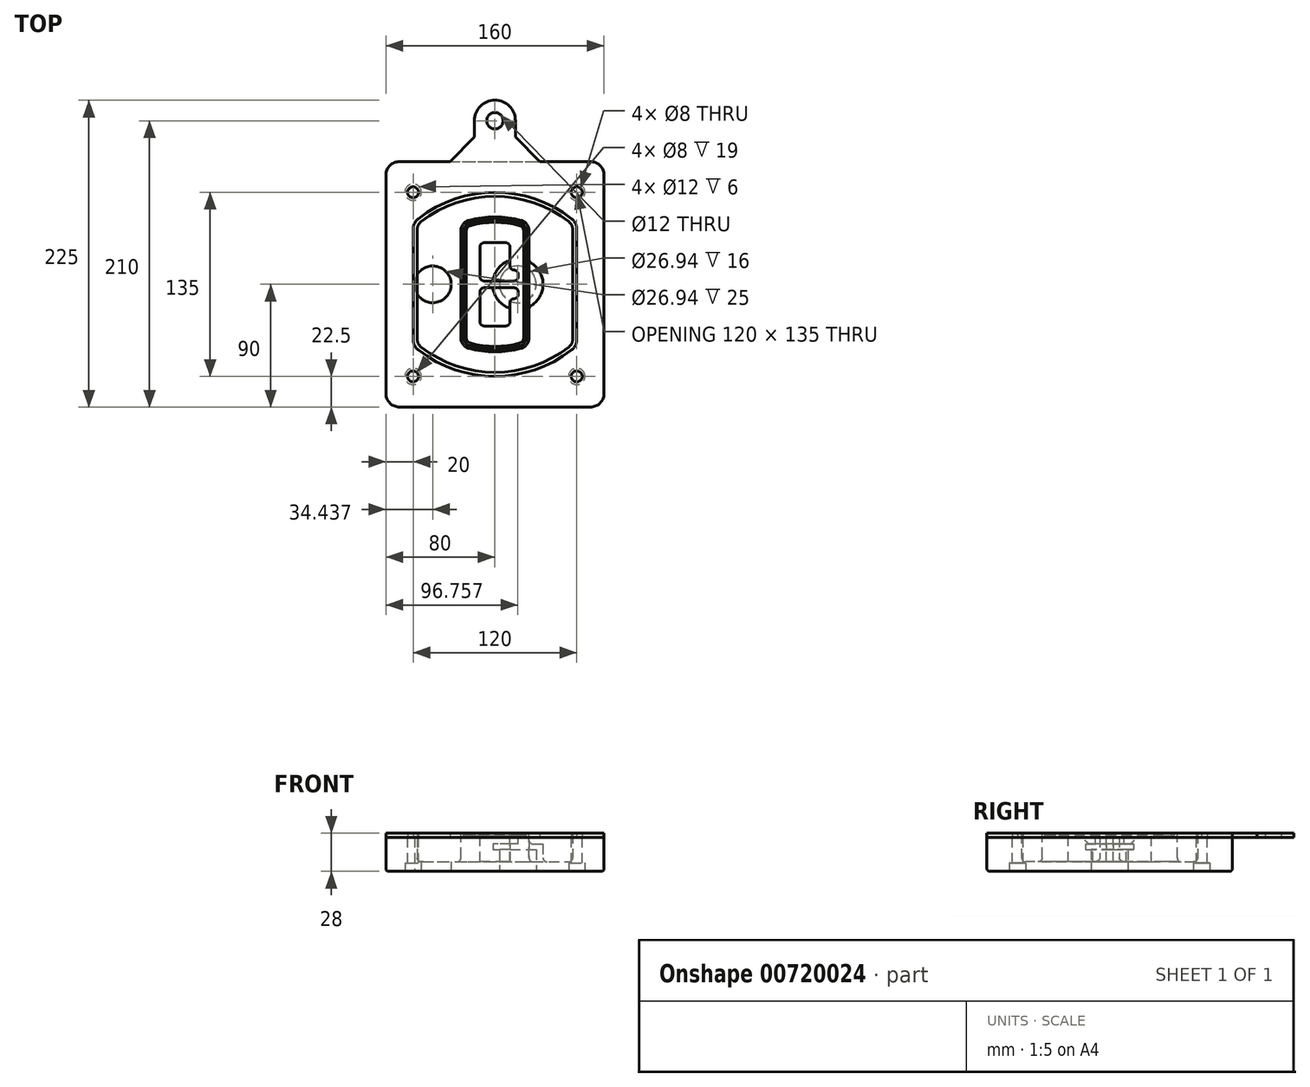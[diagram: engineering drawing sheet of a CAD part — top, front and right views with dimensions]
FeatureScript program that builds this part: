
annotation { "Feature Type Name" : "Feature", "Feature Type Description" : "" }
export const myFeature = defineFeature(function(context is Context, id is Id, definition is map)
    precondition{}
    {
        {
            var Q0;
            Q0=qCreatedBy(makeId("Top.planeOp"),FACE);
            var sketch = newSketch(context, id + "F0", { "sketchPlane" : qUnion([Q0])});
            skPoint(sketch, "E0.rect.middle", {"position": v(0, 0) * mm});
            skLineSegment(sketch, "E1.bottom", {"start": v(-70, -90) * mm, "end": v(70, -90) * mm});
            skLineSegment(sketch, "E1.top", {"start": v(-70, 90) * mm, "end": v(70, 90) * mm});
            skLineSegment(sketch, "E1.left", {"start": v(-80, -80) * mm, "end": v(-80, 80) * mm});
            skLineSegment(sketch, "E1.right", {"start": v(80, -80) * mm, "end": v(80, 80) * mm});
            skLineSegment(sketch, "E2", {"start": v(-80, 90) * mm, "end": v(80, -90) * mm, "construction": true});
            skLineSegment(sketch, "E3", {"start": v(80, 90) * mm, "end": v(-80, -90) * mm, "construction": true});
            skCircle(sketch, "E4", {"center": v(-60, 67.5) * mm, "radius": 4 * mm});
            skCircle(sketch, "E5", {"center": v(60, 67.5) * mm, "radius": 4 * mm});
            skCircle(sketch, "E6", {"center": v(60, -67.5) * mm, "radius": 4 * mm});
            skCircle(sketch, "E7", {"center": v(-60, -67.5) * mm, "radius": 4 * mm});
            skLineSegment(sketch, "E8", {"start": v(-60, 67.5) * mm, "end": v(60, 67.5) * mm, "construction": true});
            skLineSegment(sketch, "E9", {"start": v(60, 67.5) * mm, "end": v(60, -67.5) * mm, "construction": true});
            skLineSegment(sketch, "E10", {"start": v(60, -67.5) * mm, "end": v(-60, -67.5) * mm, "construction": true});
            skLineSegment(sketch, "E11", {"start": v(-60, -67.5) * mm, "end": v(-60, 67.5) * mm, "construction": true});
            skLineSegment(sketch, "E12", {"start": v(-60, 40.3) * mm, "end": v(-60, -40.3) * mm});
            skLineSegment(sketch, "E13", {"start": v(60, 40.3) * mm, "end": v(60, -40.3) * mm});
            skArc(sketch, "E14", {"start": v(56.15, 48.18) * mm, "mid": v(0, 67.5) * mm, "end": v(-56.15, 48.18) * mm});
            skArc(sketch, "E15", {"start": v(-56.15, -48.18) * mm, "mid": v(0, -67.5) * mm, "end": v(56.15, -48.18) * mm});
            skLineSegment(sketch, "E16", {"start": v(-60, 0) * mm, "end": v(60, 0) * mm, "construction": true});
            skPoint(sketch, "E17.visualSharp", {"position": v(-60, -45) * mm});
            skArc(sketch, "E17.filletArc", {"start": v(-60, -40.3) * mm, "mid": v(-58.99, -44.68) * mm, "end": v(-56.15, -48.18) * mm});
            skPoint(sketch, "E18.visualSharp", {"position": v(-60, 45) * mm});
            skArc(sketch, "E18.filletArc", {"start": v(-56.15, 48.18) * mm, "mid": v(-58.99, 44.68) * mm, "end": v(-60, 40.3) * mm});
            skPoint(sketch, "E19.visualSharp", {"position": v(60, 45) * mm});
            skArc(sketch, "E19.filletArc", {"start": v(60, 40.3) * mm, "mid": v(58.99, 44.68) * mm, "end": v(56.15, 48.18) * mm});
            skPoint(sketch, "E20.visualSharp", {"position": v(60, -45) * mm});
            skArc(sketch, "E20.filletArc", {"start": v(56.15, -48.18) * mm, "mid": v(58.99, -44.68) * mm, "end": v(60, -40.3) * mm});
            skPoint(sketch, "E21.visualSharp", {"position": v(-80, 90) * mm});
            skArc(sketch, "E21.filletArc", {"start": v(-70, 90) * mm, "mid": v(-77.07, 87.07) * mm, "end": v(-80, 80) * mm});
            skPoint(sketch, "E22.visualSharp", {"position": v(80, 90) * mm});
            skArc(sketch, "E22.filletArc", {"start": v(80, 80) * mm, "mid": v(77.07, 87.07) * mm, "end": v(70, 90) * mm});
            skPoint(sketch, "E23.visualSharp", {"position": v(80, -90) * mm});
            skArc(sketch, "E23.filletArc", {"start": v(70, -90) * mm, "mid": v(77.07, -87.07) * mm, "end": v(80, -80) * mm});
            skPoint(sketch, "E24.visualSharp", {"position": v(-80, -90) * mm});
            skArc(sketch, "E24.filletArc", {"start": v(-80, -80) * mm, "mid": v(-77.07, -87.07) * mm, "end": v(-70, -90) * mm});
            skArc(sketch, "E25.0", {"start": v(57, 40.3) * mm, "mid": v(56.3, 43.36) * mm, "end": v(54.3, 45.81) * mm});
            skLineSegment(sketch, "E25.1", {"start": v(57, 40.3) * mm, "end": v(57, -40.3) * mm});
            skArc(sketch, "E25.2", {"start": v(54.3, -45.81) * mm, "mid": v(56.3, -43.36) * mm, "end": v(57, -40.3) * mm});
            skArc(sketch, "E25.3", {"start": v(-54.3, -45.81) * mm, "mid": v(0, -64.5) * mm, "end": v(54.3, -45.81) * mm});
            skArc(sketch, "E25.4", {"start": v(-57, -40.3) * mm, "mid": v(-56.3, -43.36) * mm, "end": v(-54.3, -45.81) * mm});
            skArc(sketch, "E25.5", {"start": v(54.3, 45.81) * mm, "mid": v(0, 64.5) * mm, "end": v(-54.3, 45.81) * mm});
            skLineSegment(sketch, "E25.6", {"start": v(-57, 40.3) * mm, "end": v(-57, -40.3) * mm});
            skArc(sketch, "E25.7", {"start": v(-54.3, 45.81) * mm, "mid": v(-56.3, 43.36) * mm, "end": v(-57, 40.3) * mm});
            skArc(sketch, "E26.0", {"start": v(-58.62, 51.33) * mm, "mid": v(-62.58, 46.43) * mm, "end": v(-64, 40.3) * mm});
            skArc(sketch, "E26.1", {"start": v(58.62, 51.33) * mm, "mid": v(0, 71.5) * mm, "end": v(-58.62, 51.33) * mm});
            skArc(sketch, "E26.2", {"start": v(64, 40.3) * mm, "mid": v(62.58, 46.43) * mm, "end": v(58.62, 51.33) * mm});
            skLineSegment(sketch, "E26.3", {"start": v(64, 40.3) * mm, "end": v(64, -40.3) * mm});
            skArc(sketch, "E26.4", {"start": v(58.62, -51.33) * mm, "mid": v(62.58, -46.43) * mm, "end": v(64, -40.3) * mm});
            skLineSegment(sketch, "E26.5", {"start": v(-64, 40.3) * mm, "end": v(-64, -40.3) * mm});
            skArc(sketch, "E26.6", {"start": v(-58.62, -51.33) * mm, "mid": v(0, -71.5) * mm, "end": v(58.62, -51.33) * mm});
            skArc(sketch, "E26.7", {"start": v(-64, -40.3) * mm, "mid": v(-62.58, -46.43) * mm, "end": v(-58.62, -51.33) * mm});
            skSolve(sketch);
        }
        {
            var Q0;
            Q0=makeQuery(id+"F0.imprint","IMPRINT",FACE,{"disambiguationData":[TD([[makeQuery(id+"F0.imprint","IMPRINT",EDGE,{"derivedFrom":sQuery(id+"F0.wireOp",EDGE,"E1.bottom")}),1.0]])]});
            var Q1;
            Q1=makeQuery(id+"F0.imprint","IMPRINT",FACE,{"disambiguationData":[TD([[makeQuery(id+"F0.imprint","IMPRINT",EDGE,{"derivedFrom":sQuery(id+"F0.wireOp",EDGE,"E12")}),1.0]])]});
            var Q2;
            Q2=makeQuery(id+"F0.imprint","IMPRINT",FACE,{"disambiguationData":[TD([[makeQuery(id+"F0.imprint","IMPRINT",EDGE,{"derivedFrom":sQuery(id+"F0.wireOp",EDGE,"E25.0")}),1.0]])]});
            var Q3;
            Q3=makeQuery(id+"F0.imprint","IMPRINT",FACE,{"disambiguationData":[TD([[makeQuery(id+"F0.imprint","IMPRINT",EDGE,{"derivedFrom":sQuery(id+"F0.wireOp",EDGE,"E12")}),-1.0]])]});
            extrude(context, id + "F1", {"entities" : qUnion([Q0, Q1, Q2, Q3]), "oppositeDirection" : true, "depth" : 25 * mm});
        }
        {
            var Q0;
            Q0=makeQuery(id+"F0.imprint","IMPRINT",FACE,{"disambiguationData":[TD([[makeQuery(id+"F0.imprint","IMPRINT",EDGE,{"derivedFrom":sQuery(id+"F0.wireOp",EDGE,"E12")}),1.0]])]});
            extrude(context, id + "F2", {"entities" : qUnion([Q0]), "operationType" : NewBodyOperationType.ADD, "depth" : 3 * mm});
        }
        {
            var Q0;
            Q0=makeQuery(id+"F0.imprint","IMPRINT",FACE,{"disambiguationData":[TD([[makeQuery(id+"F0.imprint","IMPRINT",EDGE,{"derivedFrom":sQuery(id+"F0.wireOp",EDGE,"E25.0")}),1.0]])]});
            extrude(context, id + "F3", {"entities" : qUnion([Q0]), "operationType" : NewBodyOperationType.REMOVE, "oppositeDirection" : true, "depth" : 18 * mm});
        }
        {
            var Q0;
            Q0=makeQuery(id+"F2.opExtrude","CAP_FACE",FACE,{"disambiguationData":[OSD([sQuery(id+"F0.wireOp",EDGE,"E12"),sQuery(id+"F0.wireOp",EDGE,"E13"),sQuery(id+"F0.wireOp",EDGE,"E14"),sQuery(id+"F0.wireOp",EDGE,"E15"),sQuery(id+"F0.wireOp",EDGE,"E17.filletArc"),sQuery(id+"F0.wireOp",EDGE,"E18.filletArc"),sQuery(id+"F0.wireOp",EDGE,"E19.filletArc"),sQuery(id+"F0.wireOp",EDGE,"E20.filletArc"),sQuery(id+"F0.wireOp",EDGE,"E25.0"),sQuery(id+"F0.wireOp",EDGE,"E25.1"),sQuery(id+"F0.wireOp",EDGE,"E25.2"),sQuery(id+"F0.wireOp",EDGE,"E25.3"),sQuery(id+"F0.wireOp",EDGE,"E25.4"),sQuery(id+"F0.wireOp",EDGE,"E25.5"),sQuery(id+"F0.wireOp",EDGE,"E25.6"),sQuery(id+"F0.wireOp",EDGE,"E25.7")])],"isStart":false});
            var sketch = newSketch(context, id + "F4", { "sketchPlane" : qUnion([Q0])});
            skArc(sketch, "E27.0", {"start": v(-19.08, -46.97) * mm, "mid": v(0, -49.5) * mm, "end": v(19.08, -46.97) * mm});
            skArc(sketch, "E28.0", {"start": v(19.08, 46.97) * mm, "mid": v(0, 49.5) * mm, "end": v(-19.08, 46.97) * mm});
            skLineSegment(sketch, "E29", {"start": v(-25, 39.25) * mm, "end": v(-25, -39.25) * mm});
            skLineSegment(sketch, "E30", {"start": v(25, 39.25) * mm, "end": v(25, -39.25) * mm});
            skLineSegment(sketch, "E31", {"start": v(-25, 45.1) * mm, "end": v(25, 45.1) * mm, "construction": true});
            skLineSegment(sketch, "E32", {"start": v(-25, -45.1) * mm, "end": v(25, -45.1) * mm, "construction": true});
            skPoint(sketch, "E33.visualSharp", {"position": v(-25, 45.1) * mm});
            skArc(sketch, "E33.filletArc", {"start": v(-19.08, 46.97) * mm, "mid": v(-23.35, 44.11) * mm, "end": v(-25, 39.25) * mm});
            skPoint(sketch, "E34.visualSharp", {"position": v(25, 45.1) * mm});
            skArc(sketch, "E34.filletArc", {"start": v(25, 39.25) * mm, "mid": v(23.35, 44.11) * mm, "end": v(19.08, 46.97) * mm});
            skPoint(sketch, "E35.visualSharp", {"position": v(25, -45.1) * mm});
            skArc(sketch, "E35.filletArc", {"start": v(19.08, -46.97) * mm, "mid": v(23.35, -44.11) * mm, "end": v(25, -39.25) * mm});
            skPoint(sketch, "E36.visualSharp", {"position": v(-25, -45.1) * mm});
            skArc(sketch, "E36.filletArc", {"start": v(-25, -39.25) * mm, "mid": v(-23.35, -44.11) * mm, "end": v(-19.08, -46.97) * mm});
            skArc(sketch, "E37.0", {"start": v(54.3, 45.81) * mm, "mid": v(0, 64.5) * mm, "end": v(-54.3, 45.81) * mm});
            skArc(sketch, "E37.1", {"start": v(-54.3, 45.81) * mm, "mid": v(-56.3, 43.36) * mm, "end": v(-57, 40.3) * mm});
            skLineSegment(sketch, "E37.2", {"start": v(-57, 40.3) * mm, "end": v(-57, -40.3) * mm});
            skArc(sketch, "E37.3", {"start": v(-57, -40.3) * mm, "mid": v(-56.3, -43.36) * mm, "end": v(-54.3, -45.81) * mm});
            skArc(sketch, "E37.4", {"start": v(-54.3, -45.81) * mm, "mid": v(0, -64.5) * mm, "end": v(54.3, -45.81) * mm});
            skArc(sketch, "E37.5", {"start": v(54.3, -45.81) * mm, "mid": v(56.3, -43.36) * mm, "end": v(57, -40.3) * mm});
            skLineSegment(sketch, "E37.6", {"start": v(57, 40.3) * mm, "end": v(57, -40.3) * mm});
            skArc(sketch, "E37.7", {"start": v(57, 40.3) * mm, "mid": v(56.3, 43.36) * mm, "end": v(54.3, 45.81) * mm});
            skLineSegment(sketch, "E38.0", {"start": v(23, 39.25) * mm, "end": v(23, -39.25) * mm});
            skArc(sketch, "E38.1", {"start": v(18.56, -45.04) * mm, "mid": v(21.76, -42.9) * mm, "end": v(23, -39.25) * mm});
            skArc(sketch, "E38.2", {"start": v(-18.56, -45.04) * mm, "mid": v(0, -47.5) * mm, "end": v(18.56, -45.04) * mm});
            skArc(sketch, "E38.3", {"start": v(-23, -39.25) * mm, "mid": v(-21.76, -42.9) * mm, "end": v(-18.56, -45.04) * mm});
            skLineSegment(sketch, "E38.4", {"start": v(-23, 39.25) * mm, "end": v(-23, -39.25) * mm});
            skArc(sketch, "E38.5", {"start": v(23, 39.25) * mm, "mid": v(21.76, 42.9) * mm, "end": v(18.56, 45.04) * mm});
            skArc(sketch, "E38.6", {"start": v(-18.56, 45.04) * mm, "mid": v(-21.76, 42.9) * mm, "end": v(-23, 39.25) * mm});
            skArc(sketch, "E38.7", {"start": v(18.56, 45.04) * mm, "mid": v(0, 47.5) * mm, "end": v(-18.56, 45.04) * mm});
            skArc(sketch, "E39.0", {"start": v(21, 39.25) * mm, "mid": v(20.18, 41.68) * mm, "end": v(18.04, 43.1) * mm});
            skLineSegment(sketch, "E39.1", {"start": v(21, 39.25) * mm, "end": v(21, -39.25) * mm});
            skArc(sketch, "E39.2", {"start": v(18.04, -43.1) * mm, "mid": v(20.18, -41.68) * mm, "end": v(21, -39.25) * mm});
            skArc(sketch, "E39.3", {"start": v(-18.04, -43.1) * mm, "mid": v(0, -45.5) * mm, "end": v(18.04, -43.1) * mm});
            skArc(sketch, "E39.4", {"start": v(-21, -39.25) * mm, "mid": v(-20.18, -41.68) * mm, "end": v(-18.04, -43.1) * mm});
            skArc(sketch, "E39.5", {"start": v(18.04, 43.1) * mm, "mid": v(0, 45.5) * mm, "end": v(-18.04, 43.1) * mm});
            skLineSegment(sketch, "E39.6", {"start": v(-21, 39.25) * mm, "end": v(-21, -39.25) * mm});
            skArc(sketch, "E39.7", {"start": v(-18.04, 43.1) * mm, "mid": v(-20.18, 41.68) * mm, "end": v(-21, 39.25) * mm});
            skLineSegment(sketch, "E40", {"start": v(-25, 0) * mm, "end": v(25, 0) * mm, "construction": true});
            skLineSegment(sketch, "E41", {"start": v(-11, 5.5) * mm, "end": v(-11, 27.5) * mm});
            skLineSegment(sketch, "E42", {"start": v(-8, 30.5) * mm, "end": v(8, 30.5) * mm});
            skLineSegment(sketch, "E43", {"start": v(11, 27.5) * mm, "end": v(11, 13.5) * mm});
            skLineSegment(sketch, "E44", {"start": v(14, 10.5) * mm, "end": v(14, 10.5) * mm});
            skLineSegment(sketch, "E45", {"start": v(17, 7.5) * mm, "end": v(17, 5.5) * mm});
            skLineSegment(sketch, "E46", {"start": v(14, 2.5) * mm, "end": v(-8, 2.5) * mm});
            skPoint(sketch, "E47.visualSharp", {"position": v(-11, 30.5) * mm});
            skArc(sketch, "E47.filletArc", {"start": v(-8, 30.5) * mm, "mid": v(-10.12, 29.62) * mm, "end": v(-11, 27.5) * mm});
            skPoint(sketch, "E48.visualSharp", {"position": v(11, 30.5) * mm});
            skArc(sketch, "E48.filletArc", {"start": v(11, 27.5) * mm, "mid": v(10.12, 29.62) * mm, "end": v(8, 30.5) * mm});
            skPoint(sketch, "E49.visualSharp", {"position": v(11, 10.5) * mm});
            skArc(sketch, "E49.filletArc", {"start": v(11, 13.5) * mm, "mid": v(11.88, 11.38) * mm, "end": v(14, 10.5) * mm});
            skPoint(sketch, "E50.visualSharp", {"position": v(17, 10.5) * mm});
            skArc(sketch, "E50.filletArc", {"start": v(17, 7.5) * mm, "mid": v(16.12, 9.62) * mm, "end": v(14, 10.5) * mm});
            skPoint(sketch, "E51.visualSharp", {"position": v(17, 2.5) * mm});
            skArc(sketch, "E51.filletArc", {"start": v(14, 2.5) * mm, "mid": v(16.12, 3.38) * mm, "end": v(17, 5.5) * mm});
            skPoint(sketch, "E52.visualSharp", {"position": v(-11, 2.5) * mm});
            skArc(sketch, "E52.filletArc", {"start": v(-11, 5.5) * mm, "mid": v(-10.12, 3.38) * mm, "end": v(-8, 2.5) * mm});
            skLineSegment(sketch, "E53.0.MirrorCS", {"start": v(14, -2.5) * mm, "end": v(-8, -2.5) * mm});
            skArc(sketch, "E54.0.MirrorCS", {"start": v(-11, -5.5) * mm, "mid": v(-10.12, -3.38) * mm, "end": v(-8, -2.5) * mm});
            skLineSegment(sketch, "E55.0.MirrorCS", {"start": v(-11, -5.5) * mm, "end": v(-11, -27.5) * mm});
            skArc(sketch, "E56.0.MirrorCS", {"start": v(-8, -30.5) * mm, "mid": v(-10.12, -29.62) * mm, "end": v(-11, -27.5) * mm});
            skLineSegment(sketch, "E57.0.MirrorCS", {"start": v(-8, -30.5) * mm, "end": v(8, -30.5) * mm});
            skArc(sketch, "E58.0.MirrorCS", {"start": v(11, -27.5) * mm, "mid": v(10.12, -29.62) * mm, "end": v(8, -30.5) * mm});
            skLineSegment(sketch, "E59.0.MirrorCS", {"start": v(11, -27.5) * mm, "end": v(11, -13.5) * mm});
            skArc(sketch, "E60.0.MirrorCS", {"start": v(11, -13.5) * mm, "mid": v(11.88, -11.38) * mm, "end": v(14, -10.5) * mm});
            skArc(sketch, "E61.0.MirrorCS", {"start": v(17, -7.5) * mm, "mid": v(16.12, -9.62) * mm, "end": v(14, -10.5) * mm});
            skLineSegment(sketch, "E62.0.MirrorCS", {"start": v(17, -7.5) * mm, "end": v(17, -5.5) * mm});
            skArc(sketch, "E63.0.MirrorCS", {"start": v(14, -2.5) * mm, "mid": v(16.12, -3.38) * mm, "end": v(17, -5.5) * mm});
            skSolve(sketch);
        }
        {
            var Q0;
            Q0=makeQuery(id+"F4.imprint","IMPRINT",FACE,{"disambiguationData":[TD([[makeQuery(id+"F4.imprint","IMPRINT",EDGE,{"derivedFrom":sQuery(id+"F4.wireOp",EDGE,"E27.0")}),1.0]])]});
            var Q1;
            Q1=makeQuery(id+"F4.imprint","IMPRINT",FACE,{"disambiguationData":[TD([[makeQuery(id+"F4.imprint","IMPRINT",EDGE,{"derivedFrom":sQuery(id+"F4.wireOp",EDGE,"E38.0")}),-1.0]])]});
            var Q2;
            Q2=makeQuery(id+"F4.imprint","IMPRINT",FACE,{"disambiguationData":[TD([[makeQuery(id+"F4.imprint","IMPRINT",EDGE,{"derivedFrom":sQuery(id+"F4.wireOp",EDGE,"E39.0")}),1.0]])]});
            extrude(context, id + "F5", {"entities" : qUnion([Q0, Q1, Q2]), "operationType" : NewBodyOperationType.ADD, "endBound" : BoundingType.UP_TO_NEXT, "oppositeDirection" : true, "depth" : 25 * mm});
        }
        {
            var Q0;
            Q0=makeQuery(id+"F4.imprint","IMPRINT",FACE,{"disambiguationData":[TD([[makeQuery(id+"F4.imprint","IMPRINT",EDGE,{"derivedFrom":sQuery(id+"F4.wireOp",EDGE,"E38.0")}),-1.0]])]});
            extrude(context, id + "F6", {"entities" : qUnion([Q0]), "operationType" : NewBodyOperationType.REMOVE, "oppositeDirection" : true, "depth" : 2 * mm});
        }
        {
            var Q0;
            Q0=makeQuery(id+"F1.opExtrude","CAP_FACE",FACE,{"disambiguationData":[OSD([sQuery(id+"F0.wireOp",EDGE,"E1.bottom"),sQuery(id+"F0.wireOp",EDGE,"E1.top"),sQuery(id+"F0.wireOp",EDGE,"E1.left"),sQuery(id+"F0.wireOp",EDGE,"E1.right"),sQuery(id+"F0.wireOp",EDGE,"E4"),sQuery(id+"F0.wireOp",EDGE,"E5"),sQuery(id+"F0.wireOp",EDGE,"E6"),sQuery(id+"F0.wireOp",EDGE,"E7"),sQuery(id+"F0.wireOp",EDGE,"E21.filletArc"),sQuery(id+"F0.wireOp",EDGE,"E22.filletArc"),sQuery(id+"F0.wireOp",EDGE,"E23.filletArc"),sQuery(id+"F0.wireOp",EDGE,"E24.filletArc")])],"isStart":false});
            var sketch = newSketch(context, id + "F7", { "sketchPlane" : qUnion([Q0])});
            skCircle(sketch, "E64", {"center": v(16.76, 0) * mm, "radius": 13.47 * mm});
            skCircle(sketch, "E65", {"center": v(-45.56, 0) * mm, "radius": 13.47 * mm});
            skLineSegment(sketch, "E66", {"start": v(80, 0) * mm, "end": v(-80, 0) * mm});
            skCircle(sketch, "E67", {"center": v(16.76, 0) * mm, "radius": 18.47 * mm});
            skCircle(sketch, "E68", {"center": v(60, -67.5) * mm, "radius": 6 * mm});
            skCircle(sketch, "E69", {"center": v(-60, -67.5) * mm, "radius": 6 * mm});
            skCircle(sketch, "E70", {"center": v(-60, 67.5) * mm, "radius": 6 * mm});
            skCircle(sketch, "E71", {"center": v(60, 67.5) * mm, "radius": 6 * mm});
            skSolve(sketch);
        }
        {
            var Q0;
            {var subQ1=sQuery(id+"F7.wireOp",EDGE,"E66");var subQ4=sQuery(id+"F7.wireOp",EDGE,"E64");var subQ6=makeQuery(id+"F7.imprint","INTERSECT",VERTEX,{"disambiguationData":[OD(0.0)],"derivedFrom":[subQ4,subQ1]});Q0=makeQuery(id+"F7.imprint","IMPRINT",FACE,{"disambiguationData":[TD([[makeQuery(id+"F7.imprint","IMPRINT",EDGE,{"disambiguationData":[TD([[subQ6,-1.0]])],"derivedFrom":subQ4}),-1.0]])]});}
            var Q1;
            {var subQ0=sQuery(id+"F7.wireOp",EDGE,"E66");var subQ1=sQuery(id+"F7.wireOp",EDGE,"E64");var subQ3=makeQuery(id+"F7.imprint","INTERSECT",VERTEX,{"disambiguationData":[OD(0.0)],"derivedFrom":[subQ1,subQ0]});Q1=makeQuery(id+"F7.imprint","IMPRINT",FACE,{"disambiguationData":[TD([[makeQuery(id+"F7.imprint","IMPRINT",EDGE,{"disambiguationData":[TD([[subQ3,-1.0]])],"derivedFrom":subQ1}),1.0]])]});}
            var Q2;
            {var subQ0=sQuery(id+"F7.wireOp",EDGE,"E66");var subQ1=sQuery(id+"F7.wireOp",EDGE,"E64");var subQ3=makeQuery(id+"F7.imprint","INTERSECT",VERTEX,{"disambiguationData":[OD(0.0)],"derivedFrom":[subQ1,subQ0]});Q2=makeQuery(id+"F7.imprint","IMPRINT",FACE,{"disambiguationData":[TD([[makeQuery(id+"F7.imprint","IMPRINT",EDGE,{"disambiguationData":[TD([[subQ3,1.0]])],"derivedFrom":subQ1}),1.0]])]});}
            var Q3;
            {var subQ1=sQuery(id+"F7.wireOp",EDGE,"E66");var subQ4=sQuery(id+"F7.wireOp",EDGE,"E64");var subQ6=makeQuery(id+"F7.imprint","INTERSECT",VERTEX,{"disambiguationData":[OD(0.0)],"derivedFrom":[subQ4,subQ1]});Q3=makeQuery(id+"F7.imprint","IMPRINT",FACE,{"disambiguationData":[TD([[makeQuery(id+"F7.imprint","IMPRINT",EDGE,{"disambiguationData":[TD([[subQ6,1.0]])],"derivedFrom":subQ4}),-1.0]])]});}
            extrude(context, id + "F8", {"entities" : qUnion([Q0, Q1, Q2, Q3]), "operationType" : NewBodyOperationType.ADD, "oppositeDirection" : true, "depth" : 20 * mm});
        }
        {
            var Q0;
            {var subQ0=sQuery(id+"F7.wireOp",EDGE,"E66");var subQ1=sQuery(id+"F7.wireOp",EDGE,"E64");var subQ3=makeQuery(id+"F7.imprint","INTERSECT",VERTEX,{"disambiguationData":[OD(0.0)],"derivedFrom":[subQ1,subQ0]});Q0=makeQuery(id+"F7.imprint","IMPRINT",FACE,{"disambiguationData":[TD([[makeQuery(id+"F7.imprint","IMPRINT",EDGE,{"disambiguationData":[TD([[subQ3,-1.0]])],"derivedFrom":subQ1}),1.0]])]});}
            var Q1;
            {var subQ0=sQuery(id+"F7.wireOp",EDGE,"E66");var subQ1=sQuery(id+"F7.wireOp",EDGE,"E64");var subQ3=makeQuery(id+"F7.imprint","INTERSECT",VERTEX,{"disambiguationData":[OD(0.0)],"derivedFrom":[subQ1,subQ0]});Q1=makeQuery(id+"F7.imprint","IMPRINT",FACE,{"disambiguationData":[TD([[makeQuery(id+"F7.imprint","IMPRINT",EDGE,{"disambiguationData":[TD([[subQ3,1.0]])],"derivedFrom":subQ1}),1.0]])]});}
            extrude(context, id + "F9", {"entities" : qUnion([Q0, Q1]), "operationType" : NewBodyOperationType.REMOVE, "oppositeDirection" : true, "depth" : 16 * mm});
        }
        {
            var Q0;
            {var subQ0=sQuery(id+"F7.wireOp",EDGE,"E66");var subQ1=sQuery(id+"F7.wireOp",EDGE,"E65");var subQ3=makeQuery(id+"F7.imprint","INTERSECT",VERTEX,{"disambiguationData":[OD(0.0)],"derivedFrom":[subQ1,subQ0]});Q0=makeQuery(id+"F7.imprint","IMPRINT",FACE,{"disambiguationData":[TD([[makeQuery(id+"F7.imprint","IMPRINT",EDGE,{"disambiguationData":[TD([[subQ3,-1.0]])],"derivedFrom":subQ1}),1.0]])]});}
            var Q1;
            {var subQ0=sQuery(id+"F7.wireOp",EDGE,"E66");var subQ1=sQuery(id+"F7.wireOp",EDGE,"E65");var subQ3=makeQuery(id+"F7.imprint","INTERSECT",VERTEX,{"disambiguationData":[OD(0.0)],"derivedFrom":[subQ1,subQ0]});Q1=makeQuery(id+"F7.imprint","IMPRINT",FACE,{"disambiguationData":[TD([[makeQuery(id+"F7.imprint","IMPRINT",EDGE,{"disambiguationData":[TD([[subQ3,1.0]])],"derivedFrom":subQ1}),1.0]])]});}
            extrude(context, id + "F10", {"entities" : qUnion([Q0, Q1]), "operationType" : NewBodyOperationType.REMOVE, "oppositeDirection" : true, "depth" : 25 * mm});
        }
        {
            var Q0;
            Q0=makeQuery(id+"F7.imprint","IMPRINT",FACE,{"disambiguationData":[TD([[makeQuery(id+"F7.imprint","IMPRINT",EDGE,{"derivedFrom":sQuery(id+"F7.wireOp",EDGE,"E68")}),1.0]])]});
            var Q1;
            Q1=makeQuery(id+"F7.imprint","IMPRINT",FACE,{"disambiguationData":[TD([[makeQuery(id+"F7.imprint","IMPRINT",EDGE,{"derivedFrom":makeQuery(id+"F1.opExtrude","CAP_EDGE",EDGE,{"disambiguationData":[OSD([sQuery(id+"F0.wireOp",EDGE,"E5")])],"isStart":false})}),-1.0]])]});
            var Q2;
            Q2=makeQuery(id+"F7.imprint","IMPRINT",FACE,{"disambiguationData":[TD([[makeQuery(id+"F7.imprint","IMPRINT",EDGE,{"derivedFrom":sQuery(id+"F7.wireOp",EDGE,"E69")}),1.0]])]});
            var Q3;
            Q3=makeQuery(id+"F7.imprint","IMPRINT",FACE,{"disambiguationData":[TD([[makeQuery(id+"F7.imprint","IMPRINT",EDGE,{"derivedFrom":makeQuery(id+"F1.opExtrude","CAP_EDGE",EDGE,{"disambiguationData":[OSD([sQuery(id+"F0.wireOp",EDGE,"E4")])],"isStart":false})}),-1.0]])]});
            var Q4;
            Q4=makeQuery(id+"F7.imprint","IMPRINT",FACE,{"disambiguationData":[TD([[makeQuery(id+"F7.imprint","IMPRINT",EDGE,{"derivedFrom":sQuery(id+"F7.wireOp",EDGE,"E70")}),1.0]])]});
            var Q5;
            Q5=makeQuery(id+"F7.imprint","IMPRINT",FACE,{"disambiguationData":[TD([[makeQuery(id+"F7.imprint","IMPRINT",EDGE,{"derivedFrom":makeQuery(id+"F1.opExtrude","CAP_EDGE",EDGE,{"disambiguationData":[OSD([sQuery(id+"F0.wireOp",EDGE,"E7")])],"isStart":false})}),-1.0]])]});
            var Q6;
            Q6=makeQuery(id+"F7.imprint","IMPRINT",FACE,{"disambiguationData":[TD([[makeQuery(id+"F7.imprint","IMPRINT",EDGE,{"derivedFrom":sQuery(id+"F7.wireOp",EDGE,"E71")}),1.0]])]});
            var Q7;
            Q7=makeQuery(id+"F7.imprint","IMPRINT",FACE,{"disambiguationData":[TD([[makeQuery(id+"F7.imprint","IMPRINT",EDGE,{"derivedFrom":makeQuery(id+"F1.opExtrude","CAP_EDGE",EDGE,{"disambiguationData":[OSD([sQuery(id+"F0.wireOp",EDGE,"E6")])],"isStart":false})}),-1.0]])]});
            extrude(context, id + "F11", {"entities" : qUnion([Q0, Q1, Q2, Q3, Q4, Q5, Q6, Q7]), "operationType" : NewBodyOperationType.REMOVE, "oppositeDirection" : true, "depth" : 6 * mm});
        }
        {
            var Q0;
            Q0=makeQuery(id+"F9.boolean.opBoolean","COPY",FACE,{"derivedFrom":makeQuery(id+"F9.opExtrude","CAP_FACE",FACE,{"disambiguationData":[OSD([sQuery(id+"F7.wireOp",EDGE,"E64")])],"isStart":false})});
            var sketch = newSketch(context, id + "F12", { "sketchPlane" : qUnion([Q0])});
            skArc(sketch, "E72.0", {"start": v(11, 17.55) * mm, "mid": v(2.57, 11.82) * mm, "end": v(-1.54, 2.5) * mm});
            skArc(sketch, "E72.1", {"start": v(-1.54, -2.5) * mm, "mid": v(2.57, -11.82) * mm, "end": v(11, -17.55) * mm});
            skLineSegment(sketch, "E73", {"start": v(-1.54, -2.5) * mm, "end": v(14, -2.5) * mm});
            skLineSegment(sketch, "E74.0", {"start": v(14, 2.5) * mm, "end": v(-1.54, 2.5) * mm});
            skArc(sketch, "E74.1", {"start": v(14, 2.5) * mm, "mid": v(16.12, 3.38) * mm, "end": v(17, 5.5) * mm});
            skLineSegment(sketch, "E74.2", {"start": v(17, 7.5) * mm, "end": v(17, 5.5) * mm});
            skArc(sketch, "E74.3", {"start": v(17, 7.5) * mm, "mid": v(16.12, 9.62) * mm, "end": v(14, 10.5) * mm});
            skArc(sketch, "E74.4", {"start": v(11, 13.5) * mm, "mid": v(11.88, 11.38) * mm, "end": v(14, 10.5) * mm});
            skLineSegment(sketch, "E74.5", {"start": v(11, 17.55) * mm, "end": v(11, 13.5) * mm});
            skLineSegment(sketch, "E74.7", {"start": v(14, -2.5) * mm, "end": v(-1.54, -2.5) * mm});
            skArc(sketch, "E74.8", {"start": v(14, -2.5) * mm, "mid": v(16.12, -3.38) * mm, "end": v(17, -5.5) * mm});
            skLineSegment(sketch, "E74.9", {"start": v(17, -7.5) * mm, "end": v(17, -5.5) * mm});
            skArc(sketch, "E74.10", {"start": v(17, -7.5) * mm, "mid": v(16.12, -9.62) * mm, "end": v(14, -10.5) * mm});
            skArc(sketch, "E74.11", {"start": v(11, -13.5) * mm, "mid": v(11.88, -11.38) * mm, "end": v(14, -10.5) * mm});
            skLineSegment(sketch, "E74.12", {"start": v(11, -17.55) * mm, "end": v(11, -13.5) * mm});
            skPoint(sketch, "E75.orphan", {"position": v(11, -27.5) * mm});
            skPoint(sketch, "E76.orphan", {"position": v(-8, -2.5) * mm});
            skPoint(sketch, "E77.orphan", {"position": v(-8, 2.5) * mm});
            skPoint(sketch, "E78.orphan", {"position": v(11, 27.5) * mm});
            skSolve(sketch);
        }
        {
            var Q0;
            {var subQ7=sQuery(id+"F12.wireOp",EDGE,"E72.0");var subQ14=sQuery(id+"F12.wireOp",EDGE,"E72.1");var subQ16=sQuery(id+"F12.wireOp",EDGE,"E74.1");var subQ18=sQuery(id+"F12.wireOp",EDGE,"E74.8");Q0=qUnion([makeQuery(id+"F12.imprint","IMPRINT",FACE,{"disambiguationData":[TD([[makeQuery(id+"F12.imprint","IMPRINT",EDGE,{"derivedFrom":subQ7}),1.0]])]}),makeQuery(id+"F12.imprint","IMPRINT",FACE,{"disambiguationData":[TD([[makeQuery(id+"F12.imprint","IMPRINT",EDGE,{"derivedFrom":subQ14}),1.0]])]}),makeQuery(id+"F12.imprint","IMPRINT",FACE,{"disambiguationData":[TD([[makeQuery(id+"F12.imprint","IMPRINT",EDGE,{"derivedFrom":subQ16}),1.0]])]}),makeQuery(id+"F12.imprint","IMPRINT",FACE,{"disambiguationData":[TD([[makeQuery(id+"F12.imprint","IMPRINT",EDGE,{"derivedFrom":subQ18}),-1.0]])]})]);}
            var Q1;
            Q1=makeQuery(id+"F5.boolean.opBoolean","SPLIT",FACE,{"disambiguationData":[TD([makeQuery(id+"F5.opExtrude","SWEPT_FACE",FACE,{"disambiguationData":[OSD([sQuery(id+"F4.wireOp",EDGE,"E41")])]})])],"derivedFrom":makeQuery(id+"F3.boolean.opBoolean","COPY",FACE,{"derivedFrom":makeQuery(id+"F3.opExtrude","CAP_FACE",FACE,{"disambiguationData":[OSD([sQuery(id+"F0.wireOp",EDGE,"E25.0"),sQuery(id+"F0.wireOp",EDGE,"E25.1"),sQuery(id+"F0.wireOp",EDGE,"E25.2"),sQuery(id+"F0.wireOp",EDGE,"E25.3"),sQuery(id+"F0.wireOp",EDGE,"E25.4"),sQuery(id+"F0.wireOp",EDGE,"E25.5"),sQuery(id+"F0.wireOp",EDGE,"E25.6"),sQuery(id+"F0.wireOp",EDGE,"E25.7")])],"isStart":false})})});
            extrude(context, id + "F13", {"entities" : qUnion([Q0]), "operationType" : NewBodyOperationType.REMOVE, "endBound" : BoundingType.UP_TO_SURFACE, "endBoundEntityFace" : qUnion([Q1]), "depth" : 25 * mm});
        }
        {
            var Q0;
            Q0=makeQuery(id+"F3.boolean.opBoolean","COPY",EDGE,{"derivedFrom":makeQuery(id+"F3.opExtrude","CAP_EDGE",EDGE,{"disambiguationData":[OSD([sQuery(id+"F0.wireOp",EDGE,"E25.6")])],"isStart":false})});
            var Q1;
            Q1=makeQuery(id+"F8.boolean.opBoolean","INTERSECT",EDGE,{"derivedFrom":[makeQuery(id+"F5.opExtrude","SWEPT_FACE",FACE,{"disambiguationData":[OSD([sQuery(id+"F4.wireOp",EDGE,"E30")])]}),makeQuery(id+"F8.opExtrude","CAP_FACE",FACE,{"disambiguationData":[OSD([sQuery(id+"F7.wireOp",EDGE,"E67")])],"isStart":false})]});
            var Q2;
            Q2=makeQuery(id+"F8.boolean.opBoolean","INTERSECT",EDGE,{"disambiguationData":[OD(1.0)],"derivedFrom":[makeQuery(id+"F5.opExtrude","SWEPT_FACE",FACE,{"disambiguationData":[OSD([sQuery(id+"F4.wireOp",EDGE,"E30")])]}),makeQuery(id+"F8.opExtrude","SWEPT_FACE",FACE,{"disambiguationData":[OSD([sQuery(id+"F7.wireOp",EDGE,"E67")])]})]});
            var Q3;
            {var subQ0=sQuery(id+"F4.wireOp",EDGE,"E30");Q3=makeQuery(id+"F8.boolean.opBoolean","SPLIT",EDGE,{"disambiguationData":[TD([makeQuery(id+"F5.opExtrude","SWEPT_FACE",FACE,{"disambiguationData":[OSD([sQuery(id+"F4.wireOp",EDGE,"E35.filletArc")])]})])],"derivedFrom":makeQuery(id+"F5.opExtrude","CAP_EDGE",EDGE,{"disambiguationData":[OSD([subQ0])],"isStart":false})});}
            var Q4;
            {var subQ0=sQuery(id+"F0.wireOp",EDGE,"E25.7");var subQ1=sQuery(id+"F0.wireOp",EDGE,"E25.1");var subQ2=sQuery(id+"F0.wireOp",EDGE,"E25.6");var subQ3=sQuery(id+"F0.wireOp",EDGE,"E25.5");var subQ4=sQuery(id+"F0.wireOp",EDGE,"E25.4");var subQ5=sQuery(id+"F0.wireOp",EDGE,"E25.0");var subQ6=sQuery(id+"F0.wireOp",EDGE,"E25.2");var subQ7=sQuery(id+"F0.wireOp",EDGE,"E25.3");Q4=makeQuery(id+"F8.boolean.opBoolean","INTERSECT",EDGE,{"derivedFrom":[makeQuery(id+"F5.boolean.opBoolean","SPLIT",FACE,{"disambiguationData":[TD([makeQuery(id+"F2.opExtrude","SWEPT_FACE",FACE,{"disambiguationData":[OSD([subQ5])]})])],"derivedFrom":makeQuery(id+"F3.boolean.opBoolean","COPY",FACE,{"derivedFrom":makeQuery(id+"F3.opExtrude","CAP_FACE",FACE,{"disambiguationData":[OSD([subQ5,subQ1,subQ6,subQ7,subQ4,subQ3,subQ2,subQ0])],"isStart":false})})}),makeQuery(id+"F8.opExtrude","SWEPT_FACE",FACE,{"disambiguationData":[OSD([sQuery(id+"F7.wireOp",EDGE,"E67")])]})]});}
            var Q5;
            Q5=makeQuery(id+"F8.boolean.opBoolean","INTERSECT",EDGE,{"disambiguationData":[OD(0.0)],"derivedFrom":[makeQuery(id+"F5.opExtrude","SWEPT_FACE",FACE,{"disambiguationData":[OSD([sQuery(id+"F4.wireOp",EDGE,"E30")])]}),makeQuery(id+"F8.opExtrude","SWEPT_FACE",FACE,{"disambiguationData":[OSD([sQuery(id+"F7.wireOp",EDGE,"E67")])]})]});
            fillet(context, id + "F14", {"entities" : qUnion([Q0, Q1, Q2, Q3, Q4, Q5]), "radius" : 3 * mm, "tangentPropagation" : true, "allowEdgeOverflow" : false});
        }
        {
            var Q0;
            Q0=makeQuery(id+"F1.opExtrude","CAP_EDGE",EDGE,{"disambiguationData":[OSD([sQuery(id+"F0.wireOp",EDGE,"E1.bottom")])],"isStart":false});
            fillet(context, id + "F15", {"entities" : qUnion([Q0]), "radius" : 2 * mm, "tangentPropagation" : true, "allowEdgeOverflow" : false});
        }
        {
            var Q0;
            {var subQ0=sQuery(id+"F0.wireOp",EDGE,"E21.filletArc");var subQ1=sQuery(id+"F0.wireOp",EDGE,"E7");var subQ2=sQuery(id+"F0.wireOp",EDGE,"E6");var subQ3=sQuery(id+"F0.wireOp",EDGE,"E5");var subQ4=sQuery(id+"F0.wireOp",EDGE,"E4");var subQ5=sQuery(id+"F0.wireOp",EDGE,"E22.filletArc");var subQ6=sQuery(id+"F0.wireOp",EDGE,"E1.bottom");var subQ7=sQuery(id+"F0.wireOp",EDGE,"E1.right");var subQ8=sQuery(id+"F0.wireOp",EDGE,"E1.top");var subQ9=sQuery(id+"F0.wireOp",EDGE,"E1.left");var subQ10=sQuery(id+"F0.wireOp",EDGE,"E23.filletArc");var subQ11=sQuery(id+"F0.wireOp",EDGE,"E24.filletArc");Q0=makeQuery(id+"F2.boolean.opBoolean","SPLIT",FACE,{"disambiguationData":[TD([makeQuery(id+"F1.opExtrude","SWEPT_FACE",FACE,{"disambiguationData":[OSD([subQ6])]})])],"derivedFrom":makeQuery(id+"F1.opExtrude","CAP_FACE",FACE,{"disambiguationData":[OSD([subQ6,subQ8,subQ9,subQ7,subQ4,subQ3,subQ2,subQ1,subQ0,subQ5,subQ10,subQ11])],"isStart":true})});}
            var sketch = newSketch(context, id + "F16", { "sketchPlane" : qUnion([Q0])});
            skLineSegment(sketch, "E79", {"start": v(0, 90) * mm, "end": v(0, 120) * mm, "construction": true});
            skCircle(sketch, "E80", {"center": v(0, 120) * mm, "radius": 6 * mm});
            skLineSegment(sketch, "E81", {"start": v(-15, 120) * mm, "end": v(-15, 108) * mm});
            skLineSegment(sketch, "E82", {"start": v(-15, 108) * mm, "end": v(-33, 90) * mm});
            skLineSegment(sketch, "E83", {"start": v(15, 120) * mm, "end": v(15, 108) * mm});
            skLineSegment(sketch, "E84", {"start": v(15, 108) * mm, "end": v(33, 90) * mm});
            skLineSegment(sketch, "E85", {"start": v(-80, 0) * mm, "end": v(80, 0) * mm, "construction": true});
            skArc(sketch, "E86.MirrorCS", {"start": v(15, -120) * mm, "mid": v(0, -135) * mm, "end": v(-15, -120) * mm});
            skLineSegment(sketch, "E87.MirrorCS", {"start": v(0, -90) * mm, "end": v(0, -120) * mm, "construction": true});
            skLineSegment(sketch, "E88.MirrorCS", {"start": v(15, -120) * mm, "end": v(15, -108) * mm});
            skLineSegment(sketch, "E89.MirrorCS", {"start": v(-15, -120) * mm, "end": v(-15, -108) * mm});
            skCircle(sketch, "E90.MirrorC", {"center": v(0, -120) * mm, "radius": 6 * mm});
            skLineSegment(sketch, "E91.MirrorCS", {"start": v(-15, -108) * mm, "end": v(-33, -90) * mm});
            skLineSegment(sketch, "E92.MirrorCS", {"start": v(15, -108) * mm, "end": v(33, -90) * mm});
            skArc(sketch, "E93", {"start": v(15, 120) * mm, "mid": v(0, 135) * mm, "end": v(-15, 120) * mm});
            skSolve(sketch);
        }
        {
            var Q0;
            Q0=makeQuery(id+"F16.imprint","IMPRINT",FACE,{"disambiguationData":[TD([[makeQuery(id+"F16.imprint","IMPRINT",EDGE,{"derivedFrom":sQuery(id+"F16.wireOp",EDGE,"E80")}),-1.0]])]});
            var Q1;
            Q1=makeQuery(id+"F16.imprint","IMPRINT",FACE,{"disambiguationData":[TD([[makeQuery(id+"F16.imprint","IMPRINT",EDGE,{"derivedFrom":makeQuery(id+"F1.opExtrude","CAP_EDGE",EDGE,{"disambiguationData":[OSD([sQuery(id+"F0.wireOp",EDGE,"E1.left")])],"isStart":true})}),-1.0]])]});
            var Q2;
            Q2=makeQuery(id+"F16.imprint","IMPRINT",FACE,{"disambiguationData":[TD([[makeQuery(id+"F16.imprint","IMPRINT",EDGE,{"derivedFrom":sQuery(id+"F16.wireOp",EDGE,"E86.MirrorCS")}),-1.0]])]});
            var Q3;
            Q3=makeQuery(id+"F2.opExtrude","CAP_FACE",FACE,{"disambiguationData":[OSD([sQuery(id+"F0.wireOp",EDGE,"E12"),sQuery(id+"F0.wireOp",EDGE,"E13"),sQuery(id+"F0.wireOp",EDGE,"E14"),sQuery(id+"F0.wireOp",EDGE,"E15"),sQuery(id+"F0.wireOp",EDGE,"E17.filletArc"),sQuery(id+"F0.wireOp",EDGE,"E18.filletArc"),sQuery(id+"F0.wireOp",EDGE,"E19.filletArc"),sQuery(id+"F0.wireOp",EDGE,"E20.filletArc"),sQuery(id+"F0.wireOp",EDGE,"E25.0"),sQuery(id+"F0.wireOp",EDGE,"E25.1"),sQuery(id+"F0.wireOp",EDGE,"E25.2"),sQuery(id+"F0.wireOp",EDGE,"E25.3"),sQuery(id+"F0.wireOp",EDGE,"E25.4"),sQuery(id+"F0.wireOp",EDGE,"E25.5"),sQuery(id+"F0.wireOp",EDGE,"E25.6"),sQuery(id+"F0.wireOp",EDGE,"E25.7")])],"isStart":false});
            extrude(context, id + "F17", {"entities" : qUnion([Q0, Q1, Q2]), "endBound" : BoundingType.UP_TO_SURFACE, "depth" : 25 * mm, "endBoundEntityFace" : qUnion([Q3]), "offsetDistance" : 25 * mm});
        }
    });
